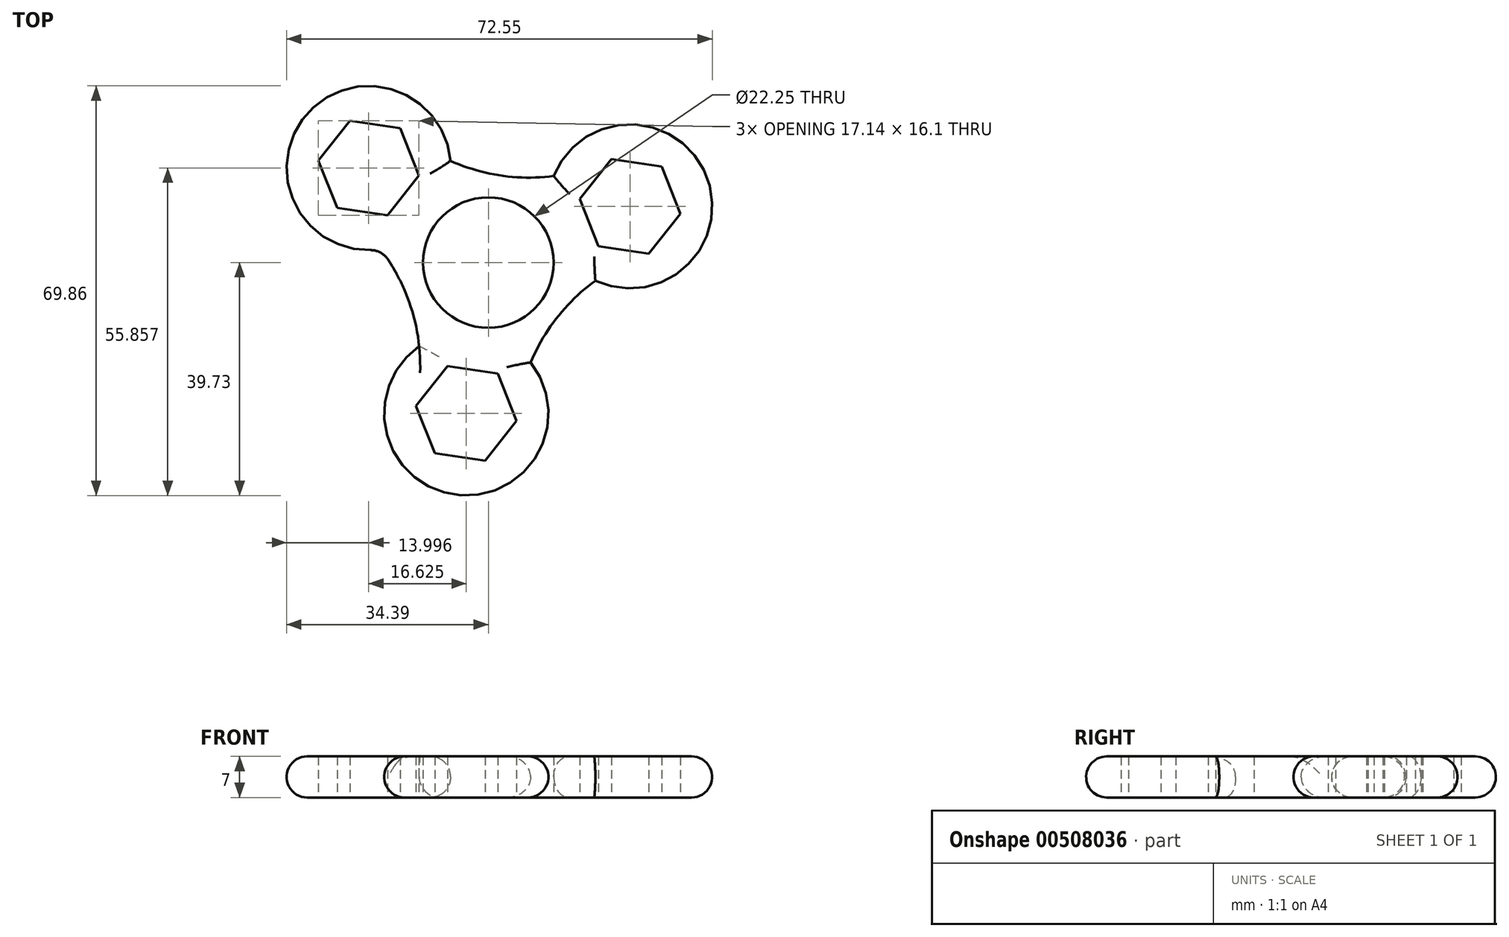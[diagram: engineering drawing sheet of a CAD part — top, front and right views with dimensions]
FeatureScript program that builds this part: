
annotation { "Feature Type Name" : "Feature", "Feature Type Description" : "" }
export const myFeature = defineFeature(function(context is Context, id is Id, definition is map)
    precondition{}
    {
        {
            var Q0;
            Q0=qCreatedBy(makeId("Top.planeOp"),FACE);
            var sketch = newSketch(context, id + "F0", { "sketchPlane" : qUnion([Q0])});
            skCircle(sketch, "E0", {"center": v(0, 0) * mm, "radius": 15 * mm});
            skCircle(sketch, "E1", {"center": v(0, 0) * mm, "radius": 11.12 * mm});
            skLineSegment(sketch, "E2", {"start": v(0, 0) * mm, "end": v(-20.4, 16.13) * mm});
            skLineSegment(sketch, "E3", {"start": v(0, 0) * mm, "end": v(24.16, 9.6) * mm});
            skLineSegment(sketch, "E4", {"start": v(0, 0) * mm, "end": v(-3.77, -25.73) * mm});
            skCircle(sketch, "E5.cCircle", {"center": v(-20.4, 16.13) * mm, "radius": 7.5 * mm, "construction": true});
            skLineSegment(sketch, "E5.0", {"start": v(-11.83, 14.87) * mm, "end": v(-17.2, 8.08) * mm});
            skLineSegment(sketch, "E5.1", {"start": v(-17.2, 8.08) * mm, "end": v(-25.77, 9.33) * mm});
            skLineSegment(sketch, "E5.2", {"start": v(-25.77, 9.33) * mm, "end": v(-28.96, 17.38) * mm});
            skLineSegment(sketch, "E5.3", {"start": v(-28.96, 17.38) * mm, "end": v(-23.6, 24.18) * mm});
            skLineSegment(sketch, "E5.4", {"start": v(-23.6, 24.18) * mm, "end": v(-15.02, 22.92) * mm});
            skLineSegment(sketch, "E5.5", {"start": v(-15.02, 22.92) * mm, "end": v(-11.83, 14.87) * mm});
            skPoint(sketch, "E5.0.midPoint", {"position": v(-14.51, 11.47) * mm});
            skCircle(sketch, "E6.cCircle", {"center": v(24.16, 9.6) * mm, "radius": 7.5 * mm, "construction": true});
            skLineSegment(sketch, "E6.0", {"start": v(18.8, 2.8) * mm, "end": v(15.6, 10.85) * mm});
            skLineSegment(sketch, "E6.1", {"start": v(15.6, 10.85) * mm, "end": v(20.97, 17.65) * mm});
            skLineSegment(sketch, "E6.2", {"start": v(20.97, 17.65) * mm, "end": v(29.54, 16.4) * mm});
            skLineSegment(sketch, "E6.3", {"start": v(29.54, 16.4) * mm, "end": v(32.73, 8.34) * mm});
            skLineSegment(sketch, "E6.4", {"start": v(32.73, 8.34) * mm, "end": v(27.36, 1.55) * mm});
            skLineSegment(sketch, "E6.5", {"start": v(27.36, 1.55) * mm, "end": v(18.8, 2.8) * mm});
            skPoint(sketch, "E6.0.midPoint", {"position": v(17.2, 6.83) * mm});
            skCircle(sketch, "E7.cCircle", {"center": v(-3.77, -25.73) * mm, "radius": 7.5 * mm, "construction": true});
            skLineSegment(sketch, "E7.0", {"start": v(-6.97, -17.68) * mm, "end": v(1.6, -18.93) * mm});
            skLineSegment(sketch, "E7.1", {"start": v(1.6, -18.93) * mm, "end": v(4.8, -26.98) * mm});
            skLineSegment(sketch, "E7.2", {"start": v(4.8, -26.98) * mm, "end": v(-0.57, -33.77) * mm});
            skLineSegment(sketch, "E7.3", {"start": v(-0.57, -33.77) * mm, "end": v(-9.14, -32.52) * mm});
            skLineSegment(sketch, "E7.4", {"start": v(-9.14, -32.52) * mm, "end": v(-12.34, -24.47) * mm});
            skLineSegment(sketch, "E7.5", {"start": v(-12.34, -24.47) * mm, "end": v(-6.97, -17.68) * mm});
            skPoint(sketch, "E7.0.midPoint", {"position": v(-2.68, -18.3) * mm});
            skArc(sketch, "E8", {"start": v(-15.02, 22.92) * mm, "mid": v(2.17, 14.84) * mm, "end": v(20.97, 17.65) * mm});
            skArc(sketch, "E9", {"start": v(27.36, 1.55) * mm, "mid": v(11.77, -9.3) * mm, "end": v(4.8, -26.98) * mm});
            skArc(sketch, "E10", {"start": v(-12.34, -24.47) * mm, "mid": v(-13.94, -5.54) * mm, "end": v(-25.77, 9.33) * mm});
            skCircle(sketch, "E11", {"center": v(-3.77, -25.73) * mm, "radius": 14 * mm});
            skCircle(sketch, "E12", {"center": v(-20.4, 16.13) * mm, "radius": 14 * mm});
            skCircle(sketch, "E13", {"center": v(24.16, 9.6) * mm, "radius": 14 * mm});
            skSolve(sketch);
        }
        {
            var Q0;
            {var subQ0=sQuery(id+"F0.wireOp",EDGE,"E8");var subQ1=sQuery(id+"F0.wireOp",EDGE,"E0");var subQ2=makeQuery(id+"F0.imprint","INTERSECT",VERTEX,{"derivedFrom":[subQ1,subQ0]});Q0=makeQuery(id+"F0.imprint","IMPRINT",FACE,{"disambiguationData":[TD([[makeQuery(id+"F0.imprint","IMPRINT",EDGE,{"disambiguationData":[TD([[subQ2,1.0]])],"derivedFrom":subQ1}),-1.0]])]});}
            var Q1;
            {var subQ0=sQuery(id+"F0.wireOp",EDGE,"E8");var subQ1=sQuery(id+"F0.wireOp",EDGE,"E0");var subQ2=makeQuery(id+"F0.imprint","INTERSECT",VERTEX,{"derivedFrom":[subQ1,subQ0]});Q1=makeQuery(id+"F0.imprint","IMPRINT",FACE,{"disambiguationData":[TD([[makeQuery(id+"F0.imprint","IMPRINT",EDGE,{"disambiguationData":[TD([[subQ2,-1.0]])],"derivedFrom":subQ1}),-1.0]])]});}
            var Q2;
            {var subQ0=sQuery(id+"F0.wireOp",EDGE,"E10");var subQ1=sQuery(id+"F0.wireOp",EDGE,"E0");var subQ2=makeQuery(id+"F0.imprint","INTERSECT",VERTEX,{"derivedFrom":[subQ1,subQ0]});Q2=makeQuery(id+"F0.imprint","IMPRINT",FACE,{"disambiguationData":[TD([[makeQuery(id+"F0.imprint","IMPRINT",EDGE,{"disambiguationData":[TD([[subQ2,1.0]])],"derivedFrom":subQ1}),-1.0]])]});}
            var Q3;
            {var subQ0=sQuery(id+"F0.wireOp",EDGE,"E10");var subQ1=sQuery(id+"F0.wireOp",EDGE,"E0");var subQ2=makeQuery(id+"F0.imprint","INTERSECT",VERTEX,{"derivedFrom":[subQ1,subQ0]});Q3=makeQuery(id+"F0.imprint","IMPRINT",FACE,{"disambiguationData":[TD([[makeQuery(id+"F0.imprint","IMPRINT",EDGE,{"disambiguationData":[TD([[subQ2,-1.0]])],"derivedFrom":subQ1}),-1.0]])]});}
            var Q4;
            {var subQ0=sQuery(id+"F0.wireOp",EDGE,"E9");var subQ1=sQuery(id+"F0.wireOp",EDGE,"E0");var subQ2=makeQuery(id+"F0.imprint","INTERSECT",VERTEX,{"derivedFrom":[subQ1,subQ0]});Q4=makeQuery(id+"F0.imprint","IMPRINT",FACE,{"disambiguationData":[TD([[makeQuery(id+"F0.imprint","IMPRINT",EDGE,{"disambiguationData":[TD([[subQ2,1.0]])],"derivedFrom":subQ1}),-1.0]])]});}
            var Q5;
            {var subQ0=sQuery(id+"F0.wireOp",EDGE,"E9");var subQ1=sQuery(id+"F0.wireOp",EDGE,"E0");var subQ2=makeQuery(id+"F0.imprint","INTERSECT",VERTEX,{"derivedFrom":[subQ1,subQ0]});Q5=makeQuery(id+"F0.imprint","IMPRINT",FACE,{"disambiguationData":[TD([[makeQuery(id+"F0.imprint","IMPRINT",EDGE,{"disambiguationData":[TD([[subQ2,-1.0]])],"derivedFrom":subQ1}),-1.0]])]});}
            var Q6;
            {var subQ5=sQuery(id+"F0.wireOp",EDGE,"E5.2");Q6=makeQuery(id+"F0.imprint","IMPRINT",FACE,{"disambiguationData":[TD([[makeQuery(id+"F0.imprint","IMPRINT",EDGE,{"derivedFrom":subQ5}),1.0]])]});}
            var Q7;
            {var subQ1=sQuery(id+"F0.wireOp",EDGE,"E6.2");Q7=makeQuery(id+"F0.imprint","IMPRINT",FACE,{"disambiguationData":[TD([[makeQuery(id+"F0.imprint","IMPRINT",EDGE,{"derivedFrom":subQ1}),1.0]])]});}
            var Q8;
            {var subQ2=sQuery(id+"F0.wireOp",EDGE,"E7.2");Q8=makeQuery(id+"F0.imprint","IMPRINT",FACE,{"disambiguationData":[TD([[makeQuery(id+"F0.imprint","IMPRINT",EDGE,{"derivedFrom":subQ2}),1.0]])]});}
            var Q9;
            {var subQ0=sQuery(id+"F0.wireOp",EDGE,"E6.5");Q9=makeQuery(id+"F0.imprint","IMPRINT",FACE,{"disambiguationData":[TD([[makeQuery(id+"F0.imprint","IMPRINT",EDGE,{"derivedFrom":subQ0}),1.0]])]});}
            var Q10;
            {var subQ0=sQuery(id+"F0.wireOp",EDGE,"E6.1");Q10=makeQuery(id+"F0.imprint","IMPRINT",FACE,{"disambiguationData":[TD([[makeQuery(id+"F0.imprint","IMPRINT",EDGE,{"derivedFrom":subQ0}),1.0]])]});}
            var Q11;
            {var subQ0=sQuery(id+"F0.wireOp",EDGE,"E5.5");Q11=makeQuery(id+"F0.imprint","IMPRINT",FACE,{"disambiguationData":[TD([[makeQuery(id+"F0.imprint","IMPRINT",EDGE,{"derivedFrom":subQ0}),1.0]])]});}
            var Q12;
            {var subQ0=sQuery(id+"F0.wireOp",EDGE,"E5.1");Q12=makeQuery(id+"F0.imprint","IMPRINT",FACE,{"disambiguationData":[TD([[makeQuery(id+"F0.imprint","IMPRINT",EDGE,{"derivedFrom":subQ0}),1.0]])]});}
            var Q13;
            {var subQ0=sQuery(id+"F0.wireOp",EDGE,"E7.5");Q13=makeQuery(id+"F0.imprint","IMPRINT",FACE,{"disambiguationData":[TD([[makeQuery(id+"F0.imprint","IMPRINT",EDGE,{"derivedFrom":subQ0}),1.0]])]});}
            var Q14;
            {var subQ0=sQuery(id+"F0.wireOp",EDGE,"E7.1");Q14=makeQuery(id+"F0.imprint","IMPRINT",FACE,{"disambiguationData":[TD([[makeQuery(id+"F0.imprint","IMPRINT",EDGE,{"derivedFrom":subQ0}),1.0]])]});}
            var Q15;
            {var subQ6=sQuery(id+"F0.wireOp",EDGE,"E0");var subQ10=makeQuery(id+"F0.imprint","INTERSECT",VERTEX,{"derivedFrom":[subQ6,sQuery(id+"F0.wireOp",EDGE,"E8")]});Q15=makeQuery(id+"F0.imprint","IMPRINT",FACE,{"disambiguationData":[TD([[makeQuery(id+"F0.imprint","IMPRINT",EDGE,{"disambiguationData":[TD([[subQ10,1.0]])],"derivedFrom":subQ6}),1.0]])]});}
            var Q16;
            {var subQ5=sQuery(id+"F0.wireOp",EDGE,"E0");var subQ6=makeQuery(id+"F0.imprint","INTERSECT",VERTEX,{"derivedFrom":[subQ5,sQuery(id+"F0.wireOp",EDGE,"E9")]});Q16=makeQuery(id+"F0.imprint","IMPRINT",FACE,{"disambiguationData":[TD([[makeQuery(id+"F0.imprint","IMPRINT",EDGE,{"disambiguationData":[TD([[subQ6,1.0]])],"derivedFrom":subQ5}),1.0]])]});}
            var Q17;
            {var subQ0=sQuery(id+"F0.wireOp",EDGE,"E12");var subQ1=sQuery(id+"F0.wireOp",EDGE,"E0");var subQ2=makeQuery(id+"F0.imprint","INTERSECT",VERTEX,{"disambiguationData":[OD(0.0)],"derivedFrom":[subQ1,subQ0]});Q17=makeQuery(id+"F0.imprint","IMPRINT",FACE,{"disambiguationData":[TD([[makeQuery(id+"F0.imprint","IMPRINT",EDGE,{"disambiguationData":[TD([[subQ2,-1.0]])],"derivedFrom":subQ1}),1.0]])]});}
            var Q18;
            {var subQ0=sQuery(id+"F0.wireOp",EDGE,"E2");var subQ1=sQuery(id+"F0.wireOp",EDGE,"E0");var subQ2=makeQuery(id+"F0.imprint","INTERSECT",VERTEX,{"derivedFrom":[subQ1,subQ0]});Q18=makeQuery(id+"F0.imprint","IMPRINT",FACE,{"disambiguationData":[TD([[makeQuery(id+"F0.imprint","IMPRINT",EDGE,{"disambiguationData":[TD([[subQ2,-1.0]])],"derivedFrom":subQ1}),1.0]])]});}
            var Q19;
            {var subQ0=sQuery(id+"F0.wireOp",EDGE,"E3");var subQ1=sQuery(id+"F0.wireOp",EDGE,"E0");var subQ2=makeQuery(id+"F0.imprint","INTERSECT",VERTEX,{"derivedFrom":[subQ1,subQ0]});Q19=makeQuery(id+"F0.imprint","IMPRINT",FACE,{"disambiguationData":[TD([[makeQuery(id+"F0.imprint","IMPRINT",EDGE,{"disambiguationData":[TD([[subQ2,1.0]])],"derivedFrom":subQ1}),1.0]])]});}
            var Q20;
            {var subQ7=sQuery(id+"F0.wireOp",EDGE,"E0");var subQ8=makeQuery(id+"F0.imprint","INTERSECT",VERTEX,{"derivedFrom":[subQ7,sQuery(id+"F0.wireOp",EDGE,"E10")]});Q20=makeQuery(id+"F0.imprint","IMPRINT",FACE,{"disambiguationData":[TD([[makeQuery(id+"F0.imprint","IMPRINT",EDGE,{"disambiguationData":[TD([[subQ8,1.0]])],"derivedFrom":subQ7}),1.0]])]});}
            var Q21;
            {var subQ0=sQuery(id+"F0.wireOp",EDGE,"E11");var subQ1=sQuery(id+"F0.wireOp",EDGE,"E0");var subQ2=makeQuery(id+"F0.imprint","INTERSECT",VERTEX,{"disambiguationData":[OD(0.0)],"derivedFrom":[subQ1,subQ0]});Q21=makeQuery(id+"F0.imprint","IMPRINT",FACE,{"disambiguationData":[TD([[makeQuery(id+"F0.imprint","IMPRINT",EDGE,{"disambiguationData":[TD([[subQ2,-1.0]])],"derivedFrom":subQ1}),1.0]])]});}
            var Q22;
            {var subQ0=sQuery(id+"F0.wireOp",EDGE,"E4");var subQ1=sQuery(id+"F0.wireOp",EDGE,"E0");var subQ2=makeQuery(id+"F0.imprint","INTERSECT",VERTEX,{"derivedFrom":[subQ1,subQ0]});Q22=makeQuery(id+"F0.imprint","IMPRINT",FACE,{"disambiguationData":[TD([[makeQuery(id+"F0.imprint","IMPRINT",EDGE,{"disambiguationData":[TD([[subQ2,-1.0]])],"derivedFrom":subQ1}),1.0]])]});}
            var Q23;
            {var subQ0=sQuery(id+"F0.wireOp",EDGE,"E3");var subQ1=sQuery(id+"F0.wireOp",EDGE,"E0");var subQ2=makeQuery(id+"F0.imprint","INTERSECT",VERTEX,{"derivedFrom":[subQ1,subQ0]});Q23=makeQuery(id+"F0.imprint","IMPRINT",FACE,{"disambiguationData":[TD([[makeQuery(id+"F0.imprint","IMPRINT",EDGE,{"disambiguationData":[TD([[subQ2,-1.0]])],"derivedFrom":subQ1}),1.0]])]});}
            extrude(context, id + "F1", {"entities" : qUnion([Q0, Q1, Q2, Q3, Q4, Q5, Q6, Q7, Q8, Q9, Q10, Q11, Q12, Q13, Q14, Q15, Q16, Q17, Q18, Q19, Q20, Q21, Q22, Q23]), "depth" : 7 * mm});
        }
        {
            var Q0;
            Q0=makeQuery(id+"F1.opExtrude","CAP_EDGE",EDGE,{"disambiguationData":[OSD([sQuery(id+"F0.wireOp",EDGE,"E12")])],"isStart":false});
            var Q1;
            Q1=makeQuery(id+"F1.opExtrude","SWEPT_EDGE",EDGE,{"disambiguationData":[OSD([sQuery(id+"F0.wireOp",EDGE,"E10"),sQuery(id+"F0.wireOp",EDGE,"E12")])]});
            var Q2;
            Q2=makeQuery(id+"F1.opExtrude","CAP_EDGE",EDGE,{"disambiguationData":[OSD([sQuery(id+"F0.wireOp",EDGE,"E8")])],"isStart":false});
            var Q3;
            Q3=makeQuery(id+"F1.opExtrude","CAP_EDGE",EDGE,{"disambiguationData":[OSD([sQuery(id+"F0.wireOp",EDGE,"E9")])],"isStart":false});
            var Q4;
            Q4=makeQuery(id+"F1.opExtrude","CAP_EDGE",EDGE,{"disambiguationData":[OSD([sQuery(id+"F0.wireOp",EDGE,"E11")])],"isStart":false});
            var Q5;
            Q5=makeQuery(id+"F1.opExtrude","CAP_EDGE",EDGE,{"disambiguationData":[OSD([sQuery(id+"F0.wireOp",EDGE,"E13")])],"isStart":false});
            var Q6;
            Q6=makeQuery(id+"F1.opExtrude","CAP_EDGE",EDGE,{"disambiguationData":[OSD([sQuery(id+"F0.wireOp",EDGE,"E9")])],"isStart":true});
            var Q7;
            Q7=makeQuery(id+"F1.opExtrude","CAP_EDGE",EDGE,{"disambiguationData":[OSD([sQuery(id+"F0.wireOp",EDGE,"E11")])],"isStart":true});
            var Q8;
            Q8=makeQuery(id+"F1.opExtrude","CAP_EDGE",EDGE,{"disambiguationData":[OSD([sQuery(id+"F0.wireOp",EDGE,"E13")])],"isStart":true});
            var Q9;
            Q9=makeQuery(id+"F1.opExtrude","CAP_EDGE",EDGE,{"disambiguationData":[OSD([sQuery(id+"F0.wireOp",EDGE,"E8")])],"isStart":true});
            var Q10;
            Q10=makeQuery(id+"F1.opExtrude","CAP_EDGE",EDGE,{"disambiguationData":[OSD([sQuery(id+"F0.wireOp",EDGE,"E10")])],"isStart":true});
            var Q11;
            Q11=makeQuery(id+"F1.opExtrude","CAP_EDGE",EDGE,{"disambiguationData":[OSD([sQuery(id+"F0.wireOp",EDGE,"E12")])],"isStart":true});
            fillet(context, id + "F2", {"entities" : qUnion([Q0, Q1, Q2, Q3, Q4, Q5, Q6, Q7, Q8, Q9, Q10, Q11]), "radius" : 3.5 * mm, "tangentPropagation" : true, "allowEdgeOverflow" : false});
        }
    });
